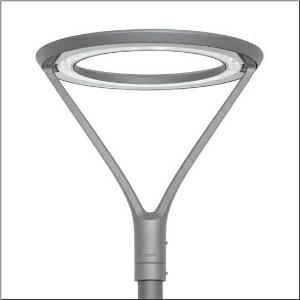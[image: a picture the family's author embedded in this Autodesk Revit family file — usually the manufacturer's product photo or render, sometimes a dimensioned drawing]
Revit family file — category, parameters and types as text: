
# Revit family: dl_r__20_led___p1_0a_5xa51283wr008p_f4bb
name_source: partatom
category: Lighting Fixtures
units: mm (PartAtom-declared; Revit-internal decimal feet)

## family parameters
Cut with Voids When Loaded = No
Host = Face
Light Source = No
Part Type = Normal
Room Calculation Point = No
Round Connector Dimension = Use Diameter
Shared = No

## types (1)
- --- (1 x LED 3000K / CRI = 80 (unbekannt), 4240 lm, 3000K)
    Apparent Load = 53 VA
    CIE Flux Codes = 31 71 96 100 100
    Color Rendering = 80
    Color Temperature = 3000K
    Default Elevation = 1800 mm
    Description = DL® 20 LED, mast luminaire, primary light control with cycle path optic, highly specular, primary optical cover: cover, of toughened safety glass of clear glass with excellent transmission level, light distribution: P1.0a, light emission: direct distribution, primary light characteristic: asymmetric, installation type: post-top, LED High Power LED, rated luminous flux: 4.240 lm, light colour: 830, colour temperature: 3000K, control gear: ECG Plus, control: overheat protection, power reduction, digital communication interface, constant luminous flux control, time-dependent luminous flux control, flexible luminous flux parameterisation, electronic power reduction, mains connection: 220..240V, 50/60Hz, connection cable pre-assembled, cable length: 5 m, start of lifetime: 53 W, end of lifetime: 54 W, reduction: 24 W, luminaire housing, upper part, of cast aluminium, powder-coated, Siteco® metallic grey (DB 702S), diameter: 690 mm, height: 690mm, spigot size: 76mm (post-top), luminaire housing, of cast aluminium, powder-coated, Siteco® metallic grey (DB 702S), protection rating (complete): IP66, insulation class (complete): insulation class II (safety insulation), certification: CE, ENEC, VDE, impact resistance: IK08, permissible ambient temperature for indoor applications: -25..+30°C, standard-compliant lighting for roads and squares, packaging unit: 1 piece

Light Distribution: P1.0a
    Height = 690 mm
    Lamp = 1 x LED 3000K / CRI >= 80 (unbekannt)
    Lamp Light Flux = 4240 lm
    Lamp count = 1
    Length = 690 mm
    Luminous efficacy = 80 lm/W
    Manufacturer = Siteco
    ModVariant = No
    Model = 5XA51283WR008P
    Number of Poles = 1
    OnlyDefault = Yes
    Power Factor = 1
    Product Name = DL® 20 LED | P1.0a
    Product group = mast luminaire | pylon top
    ProductGroupID = 6100
    Protection Class = Protection class II
    Protection Degree = IP 66
    RLX_Detail_Level = 1
    RlxData = <blob elided: 206581 chars, md5=c2e1c00e>
    Socket = socket
    Standby Power = 0 W
    System Light Flux = 4240 lm
    System Power = 53 W
    Type Comments = factory setting: luminous flux: 100 % | dim-lin: 254 | 683 mA
    Type Image = l_1006001.jpg
    URL = http://relux.com
    VarID = @adj_141243
    Voltage = 0 V
    Weight = 0.00 kg
    Width = 0 mm  [stored 0 ft]

note: [stored X ft] marks values corroborated as IEEE doubles in the binary element streams (Revit-internal decimal feet)

## geometry (parser evidence)
native form markers: Blend x4, Sweep x10
no freeform markers — native parametric forms only
